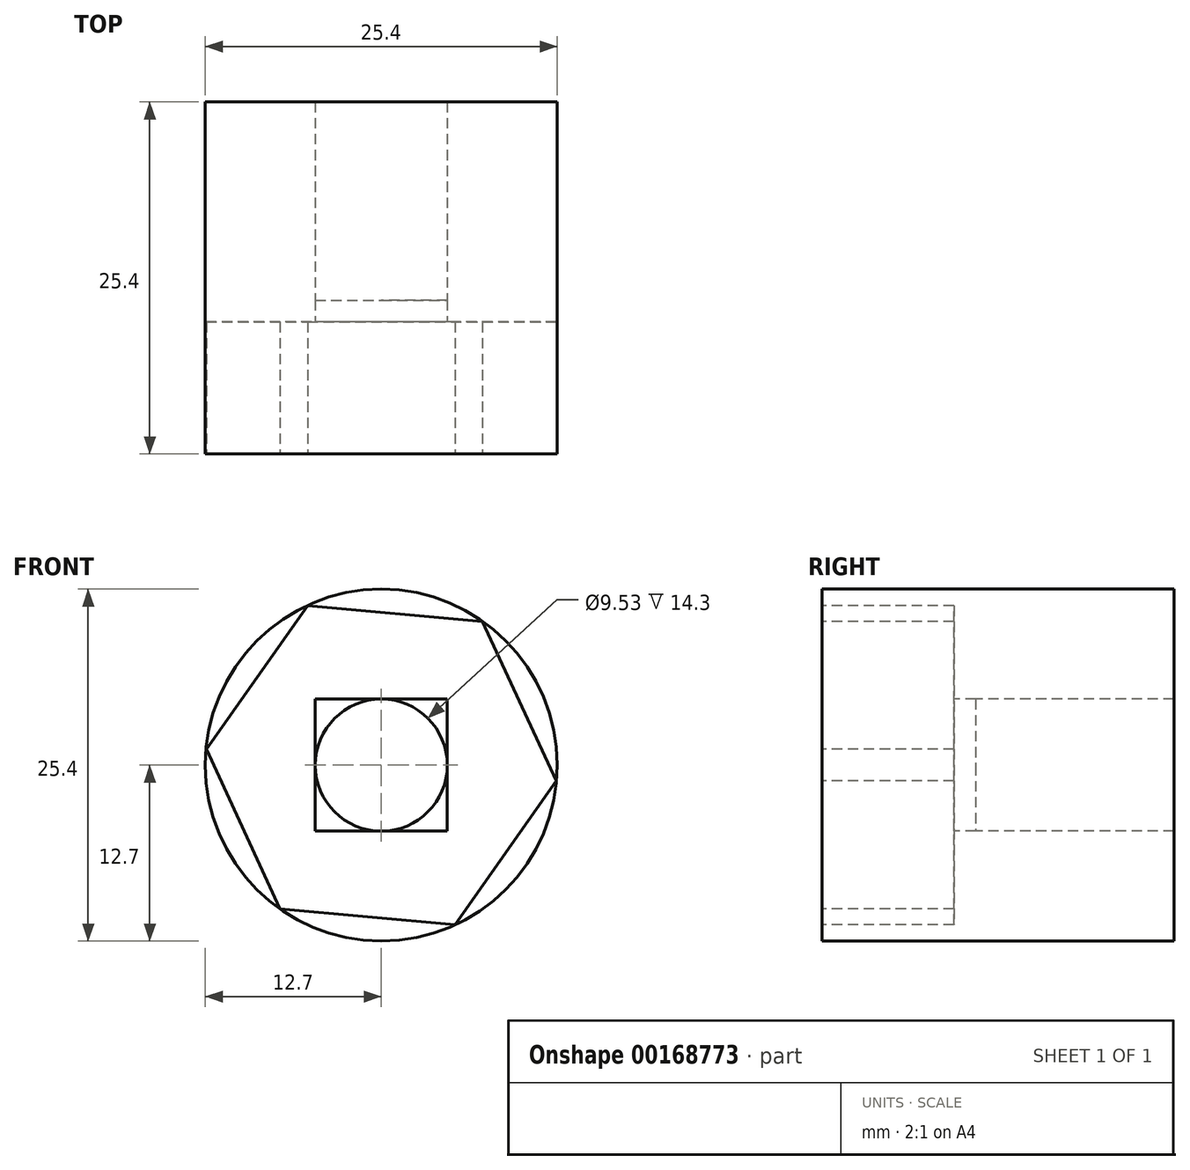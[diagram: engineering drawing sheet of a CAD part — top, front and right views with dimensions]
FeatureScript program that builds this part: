
annotation { "Feature Type Name" : "Feature", "Feature Type Description" : "" }
export const myFeature = defineFeature(function(context is Context, id is Id, definition is map)
    precondition{}
    {
        {
            var Q0;
            Q0=qCreatedBy(makeId("Front.planeOp"),FACE);
            var sketch = newSketch(context, id + "F0", { "sketchPlane" : qUnion([Q0])});
            skCircle(sketch, "E0", {"center": v(0, 0) * mm, "radius": 12.7 * mm});
            skSolve(sketch);
        }
        {
            var Q0;
            Q0 = qSketchRegion(id + "F0", true);
            extrude(context, id + "F1", {"entities" : qUnion([Q0]), "depth" : 25.4 * mm});
        }
        {
            var Q0;
            Q0=makeQuery(id+"F1.opExtrude","CAP_FACE",FACE,{"disambiguationData":[OSD([sQuery(id+"F0.wireOp",EDGE,"E0")])],"isStart":false});
            var sketch = newSketch(context, id + "F2", { "sketchPlane" : qUnion([Q0])});
            skLineSegment(sketch, "E1.bottom", {"start": v(-4.76, 4.76) * mm, "end": v(4.76, 4.76) * mm});
            skLineSegment(sketch, "E1.top", {"start": v(-4.76, -4.76) * mm, "end": v(4.76, -4.76) * mm});
            skLineSegment(sketch, "E1.left", {"start": v(-4.76, 4.76) * mm, "end": v(-4.76, -4.76) * mm});
            skLineSegment(sketch, "E1.right", {"start": v(4.76, 4.76) * mm, "end": v(4.76, -4.76) * mm});
            skPoint(sketch, "E1.middle", {"position": v(0, 0) * mm});
            skCircle(sketch, "E2", {"center": v(0, 0) * mm, "radius": 4.76 * mm});
            skSolve(sketch);
        }
        {
            var Q0;
            {var subQ0=sQuery(id+"F2.wireOp",EDGE,"E2");var subQ1=makeQuery(id+"F2.imprint","INTERSECT",VERTEX,{"derivedFrom":[sQuery(id+"F2.wireOp",EDGE,"E1.bottom"),subQ0]});Q0=makeQuery(id+"F2.imprint","IMPRINT",FACE,{"disambiguationData":[TD([[makeQuery(id+"F2.imprint","IMPRINT",EDGE,{"disambiguationData":[TD([[subQ1,1.0]])],"derivedFrom":subQ0}),1.0]])]});}
            extrude(context, id + "F3", {"entities" : qUnion([Q0]), "operationType" : NewBodyOperationType.REMOVE, "endBound" : BoundingType.THROUGH_ALL, "oppositeDirection" : true, "depth" : 25.4 * mm});
        }
        {
            var Q0;
            Q0 = qSketchRegion(id + "F2", true);
            extrude(context, id + "F4", {"entities" : qUnion([Q0]), "operationType" : NewBodyOperationType.REMOVE, "oppositeDirection" : true, "depth" : 11.1 * mm});
        }
        {
            var Q0;
            Q0=makeQuery(id+"F1.opExtrude","CAP_FACE",FACE,{"disambiguationData":[OSD([sQuery(id+"F0.wireOp",EDGE,"E0")])],"isStart":false});
            var sketch = newSketch(context, id + "F5", { "sketchPlane" : qUnion([Q0])});
            skCircle(sketch, "E3.cCircle", {"center": v(0, 0) * mm, "radius": 10.98 * mm, "construction": true});
            skLineSegment(sketch, "E3.0", {"start": v(-7.3, -10.36) * mm, "end": v(-12.62, 1.14) * mm});
            skLineSegment(sketch, "E3.1", {"start": v(-12.62, 1.14) * mm, "end": v(-5.32, 11.5) * mm});
            skLineSegment(sketch, "E3.2", {"start": v(-5.32, 11.5) * mm, "end": v(7.3, 10.36) * mm});
            skLineSegment(sketch, "E3.3", {"start": v(7.3, 10.36) * mm, "end": v(12.62, -1.14) * mm});
            skLineSegment(sketch, "E3.4", {"start": v(12.62, -1.14) * mm, "end": v(5.32, -11.5) * mm});
            skLineSegment(sketch, "E3.5", {"start": v(5.32, -11.5) * mm, "end": v(-7.3, -10.36) * mm});
            skPoint(sketch, "E3.0.midPoint", {"position": v(-9.96, -4.6) * mm});
            skSolve(sketch);
        }
        {
            var Q0;
            Q0 = qSketchRegion(id + "F5", true);
            extrude(context, id + "F6", {"entities" : qUnion([Q0]), "operationType" : NewBodyOperationType.REMOVE, "oppositeDirection" : true, "depth" : 9.52 * mm});
        }
    });
